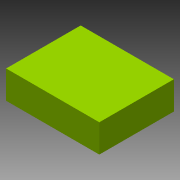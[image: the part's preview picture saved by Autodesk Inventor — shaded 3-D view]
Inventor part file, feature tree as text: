
AUTODESK INVENTOR PART (.ipt)
format: ipt  version: 2015 (Build 190159000, 159)  size: 81,920 bytes
history: native  units: mm
features: other x1, extrude x1, sketch x1
ambient origin geometry x8: Origin, YZ Plane, XZ Plane, XY Plane, X Axis, Y Axis, Z Axis, Center Point
bodies: Body1 (feature_tree)
feature tree (3):
  other  "ソリッド1"
  extrude  "押し出し1"  Depth=100.0mm
  sketch  "スケッチ1"
